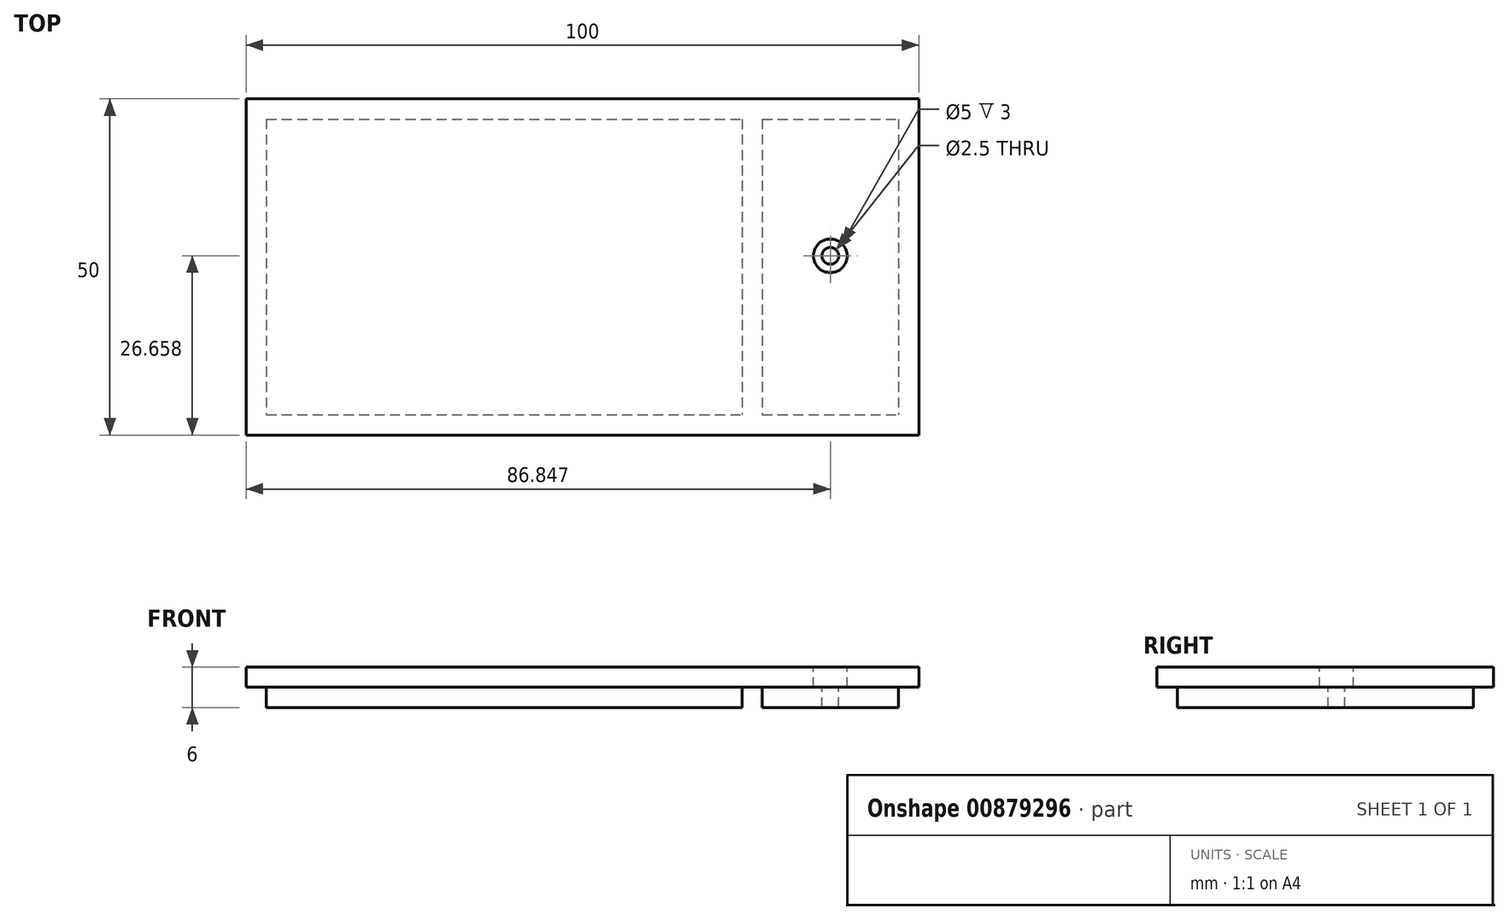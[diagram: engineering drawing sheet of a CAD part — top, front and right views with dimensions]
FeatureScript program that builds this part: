
annotation { "Feature Type Name" : "Feature", "Feature Type Description" : "" }
export const myFeature = defineFeature(function(context is Context, id is Id, definition is map)
    precondition{}
    {
        {
            var Q0;
            Q0=qCreatedBy(makeId("Top.planeOp"),FACE);
            var sketch = newSketch(context, id + "F0", { "sketchPlane" : qUnion([Q0])});
            skLineSegment(sketch, "E0.0", {"start": v(-100, 50) * mm, "end": v(0, 50) * mm});
            skLineSegment(sketch, "E1.0", {"start": v(-100, 0) * mm, "end": v(-100, 50) * mm});
            skLineSegment(sketch, "E2.0", {"start": v(-100, 0) * mm, "end": v(0, 0) * mm});
            skLineSegment(sketch, "E3.0", {"start": v(0, 0) * mm, "end": v(0, 50) * mm});
            skLineSegment(sketch, "E4.0", {"start": v(-3, 47) * mm, "end": v(-3, 3) * mm});
            skLineSegment(sketch, "E5.0", {"start": v(-23.28, 47) * mm, "end": v(-3, 47) * mm});
            skLineSegment(sketch, "E6.0", {"start": v(-23.28, 47) * mm, "end": v(-23.28, 3) * mm});
            skLineSegment(sketch, "E7.0", {"start": v(-23.28, 3) * mm, "end": v(-3, 3) * mm});
            skLineSegment(sketch, "E8.0", {"start": v(-26.28, 47) * mm, "end": v(-26.28, 3) * mm});
            skLineSegment(sketch, "E9.0", {"start": v(-97, 47) * mm, "end": v(-26.28, 47) * mm});
            skLineSegment(sketch, "E10.0", {"start": v(-97, 47) * mm, "end": v(-97, 3) * mm});
            skLineSegment(sketch, "E11.0", {"start": v(-97, 3) * mm, "end": v(-26.28, 3) * mm});
            skSolve(sketch);
        }
        {
            var Q0;
            Q0=makeQuery(id+"F0.imprint","IMPRINT",FACE,{"disambiguationData":[TD([[makeQuery(id+"F0.imprint","IMPRINT",EDGE,{"derivedFrom":sQuery(id+"F0.wireOp",EDGE,"E8.0")}),-1.0]])]});
            var Q1;
            Q1=makeQuery(id+"F0.imprint","IMPRINT",FACE,{"disambiguationData":[TD([[makeQuery(id+"F0.imprint","IMPRINT",EDGE,{"derivedFrom":sQuery(id+"F0.wireOp",EDGE,"E4.0")}),-1.0]])]});
            var Q2;
            Q2=makeQuery(id+"F0.imprint","IMPRINT",FACE,{"disambiguationData":[TD([[makeQuery(id+"F0.imprint","IMPRINT",EDGE,{"derivedFrom":sQuery(id+"F0.wireOp",EDGE,"E0.0")}),-1.0]])]});
            extrude(context, id + "F1", {"entities" : qUnion([Q0, Q1, Q2]), "depth" : 3 * mm, "offsetDistance" : 25 * mm});
        }
        {
            var Q0;
            Q0=makeQuery(id+"F0.imprint","IMPRINT",FACE,{"disambiguationData":[TD([[makeQuery(id+"F0.imprint","IMPRINT",EDGE,{"derivedFrom":sQuery(id+"F0.wireOp",EDGE,"E8.0")}),-1.0]])]});
            var Q1;
            Q1=makeQuery(id+"F0.imprint","IMPRINT",FACE,{"disambiguationData":[TD([[makeQuery(id+"F0.imprint","IMPRINT",EDGE,{"derivedFrom":sQuery(id+"F0.wireOp",EDGE,"E4.0")}),-1.0]])]});
            extrude(context, id + "F2", {"entities" : qUnion([Q0, Q1]), "operationType" : NewBodyOperationType.ADD, "oppositeDirection" : true, "depth" : 3 * mm, "offsetDistance" : 25 * mm});
        }
        {
            var Q0;
            Q0=makeQuery(id+"F1.opExtrude","CAP_FACE",FACE,{"disambiguationData":[OSD([sQuery(id+"F0.wireOp",EDGE,"E0.0"),sQuery(id+"F0.wireOp",EDGE,"E1.0"),sQuery(id+"F0.wireOp",EDGE,"E2.0"),sQuery(id+"F0.wireOp",EDGE,"E3.0")])],"isStart":false});
            var sketch = newSketch(context, id + "F3", { "sketchPlane" : qUnion([Q0])});
            skCircle(sketch, "E12", {"center": v(-13.15, 26.66) * mm, "radius": 2.5 * mm});
            skSolve(sketch);
        }
        {
            var Q0;
            Q0=makeQuery(id+"F3.imprint","IMPRINT",FACE,{"disambiguationData":[TD([[makeQuery(id+"F3.imprint","IMPRINT",EDGE,{"derivedFrom":sQuery(id+"F3.wireOp",EDGE,"E12")}),1.0]])]});
            extrude(context, id + "F4", {"entities" : qUnion([Q0]), "operationType" : NewBodyOperationType.REMOVE, "oppositeDirection" : true, "depth" : 3 * mm, "offsetDistance" : 25 * mm});
        }
        {
            var Q0;
            Q0=makeQuery(id+"F0.imprint","IMPRINT",FACE,{"disambiguationData":[TD([[makeQuery(id+"F0.imprint","IMPRINT",EDGE,{"derivedFrom":sQuery(id+"F0.wireOp",EDGE,"E4.0")}),-1.0]])]});
            var sketch = newSketch(context, id + "F5", { "sketchPlane" : qUnion([Q0])});
            skCircle(sketch, "E13", {"center": v(-13.15, 26.66) * mm, "radius": 1.25 * mm});
            skCircle(sketch, "E14.0", {"center": v(-13.15, 26.66) * mm, "radius": 2.5 * mm});
            skSolve(sketch);
        }
        {
            var Q0;
            Q0=makeQuery(id+"F5.imprint","IMPRINT",FACE,{"disambiguationData":[TD([[makeQuery(id+"F5.imprint","IMPRINT",EDGE,{"derivedFrom":sQuery(id+"F5.wireOp",EDGE,"E13")}),1.0]])]});
            extrude(context, id + "F6", {"entities" : qUnion([Q0]), "operationType" : NewBodyOperationType.REMOVE, "oppositeDirection" : true, "depth" : 25 * mm, "offsetDistance" : 25 * mm});
        }
    });
